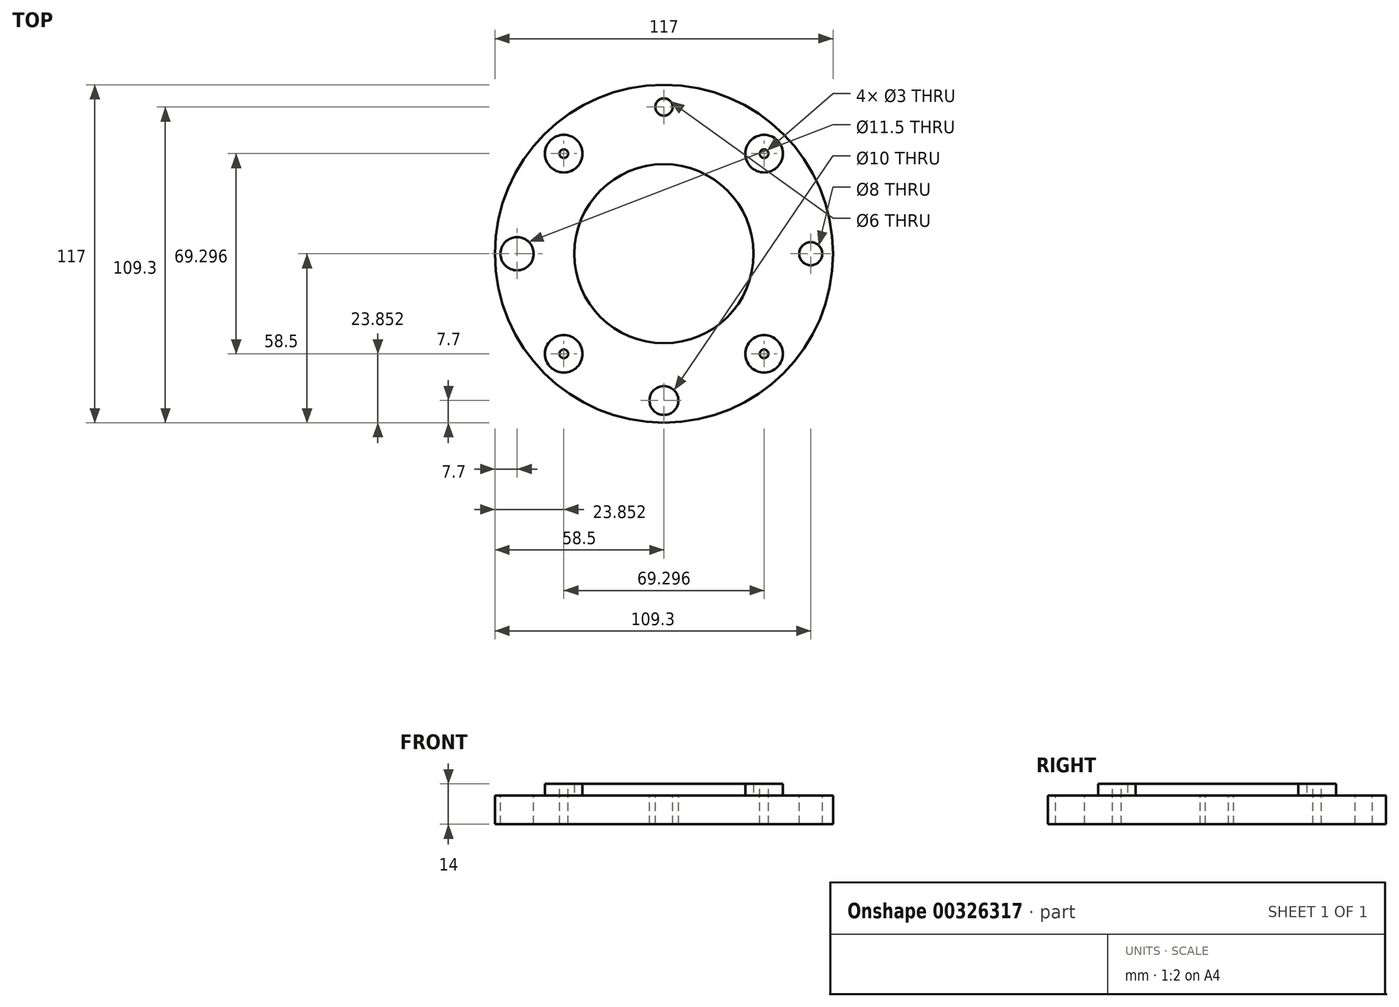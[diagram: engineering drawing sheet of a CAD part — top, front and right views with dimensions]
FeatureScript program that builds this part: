
annotation { "Feature Type Name" : "Feature", "Feature Type Description" : "" }
export const myFeature = defineFeature(function(context is Context, id is Id, definition is map)
    precondition{}
    {
        {
            var Q0;
            Q0=qCreatedBy(makeId("Top.planeOp"),FACE);
            var sketch = newSketch(context, id + "F0", { "sketchPlane" : qUnion([Q0])});
            skCircle(sketch, "E0", {"center": v(0, 0) * mm, "radius": 58.5 * mm});
            skCircle(sketch, "E1", {"center": v(0, 0) * mm, "radius": 50.8 * mm, "construction": true});
            skCircle(sketch, "E2", {"center": v(0, 50.8) * mm, "radius": 5.75 * mm, "construction": true});
            skCircle(sketch, "E3.1.0", {"center": v(-50.8, 0) * mm, "radius": 5.75 * mm, "construction": true});
            skCircle(sketch, "E3.2.0", {"center": v(0, -50.8) * mm, "radius": 5.75 * mm, "construction": true});
            skCircle(sketch, "E3.3.0", {"center": v(50.8, 0) * mm, "radius": 5.75 * mm, "construction": true});
            skCircle(sketch, "E4", {"center": v(0, 0) * mm, "radius": 61.85 * mm, "construction": true});
            skCircle(sketch, "E5", {"center": v(0, 0) * mm, "radius": 63.5 * mm});
            skCircle(sketch, "E6", {"center": v(0, 0) * mm, "radius": 49 * mm, "construction": true});
            skCircle(sketch, "E7", {"center": v(34.65, 34.65) * mm, "radius": 6.5 * mm});
            skCircle(sketch, "E8.1.0", {"center": v(-34.65, 34.65) * mm, "radius": 6.5 * mm});
            skCircle(sketch, "E8.2.0", {"center": v(-34.65, -34.65) * mm, "radius": 6.5 * mm});
            skCircle(sketch, "E8.3.0", {"center": v(34.65, -34.65) * mm, "radius": 6.5 * mm});
            skCircle(sketch, "E9", {"center": v(0, 0) * mm, "radius": 35.25 * mm, "construction": true});
            skCircle(sketch, "E10", {"center": v(0, 0) * mm, "radius": 31 * mm});
            skCircle(sketch, "E11", {"center": v(49, 0) * mm, "radius": 4.25 * mm, "construction": true});
            skCircle(sketch, "E12", {"center": v(-49, 0) * mm, "radius": 4.25 * mm, "construction": true});
            skCircle(sketch, "E13", {"center": v(0, 50.8) * mm, "radius": 3 * mm});
            skCircle(sketch, "E14", {"center": v(50.8, 0) * mm, "radius": 4 * mm});
            skCircle(sketch, "E15", {"center": v(0, -50.8) * mm, "radius": 5 * mm});
            skCircle(sketch, "E16", {"center": v(-50.8, 0) * mm, "radius": 5.75 * mm});
            skCircle(sketch, "E17", {"center": v(-34.65, 34.65) * mm, "radius": 1.5 * mm});
            skCircle(sketch, "E18", {"center": v(34.65, 34.65) * mm, "radius": 1.5 * mm});
            skCircle(sketch, "E19", {"center": v(-34.65, -34.65) * mm, "radius": 1.5 * mm});
            skCircle(sketch, "E20", {"center": v(34.65, -34.65) * mm, "radius": 1.5 * mm});
            skCircle(sketch, "E21", {"center": v(0, 50.8) * mm, "radius": 9 * mm, "construction": true});
            skSolve(sketch);
        }
        {
            var Q0;
            Q0=makeQuery(id+"F0.imprint","IMPRINT",FACE,{"disambiguationData":[TD([[makeQuery(id+"F0.imprint","IMPRINT",EDGE,{"derivedFrom":sQuery(id+"F0.wireOp",EDGE,"E0")}),1.0]])]});
            var Q1;
            Q1=makeQuery(id+"F0.imprint","IMPRINT",FACE,{"disambiguationData":[TD([[makeQuery(id+"F0.imprint","IMPRINT",EDGE,{"derivedFrom":sQuery(id+"F0.wireOp",EDGE,"E8.1.0")}),1.0]])]});
            var Q2;
            Q2=makeQuery(id+"F0.imprint","IMPRINT",FACE,{"disambiguationData":[TD([[makeQuery(id+"F0.imprint","IMPRINT",EDGE,{"derivedFrom":sQuery(id+"F0.wireOp",EDGE,"E7")}),1.0]])]});
            var Q3;
            Q3=makeQuery(id+"F0.imprint","IMPRINT",FACE,{"disambiguationData":[TD([[makeQuery(id+"F0.imprint","IMPRINT",EDGE,{"derivedFrom":sQuery(id+"F0.wireOp",EDGE,"E8.3.0")}),1.0]])]});
            var Q4;
            Q4=makeQuery(id+"F0.imprint","IMPRINT",FACE,{"disambiguationData":[TD([[makeQuery(id+"F0.imprint","IMPRINT",EDGE,{"derivedFrom":sQuery(id+"F0.wireOp",EDGE,"E8.2.0")}),1.0]])]});
            var Q5;
            Q5=makeQuery(id+"F0.imprint","IMPRINT",FACE,{"disambiguationData":[TD([[makeQuery(id+"F0.imprint","IMPRINT",EDGE,{"derivedFrom":sQuery(id+"F0.wireOp",EDGE,"E10")}),1.0]])]});
            extrude(context, id + "F1", {"entities" : qUnion([Q0, Q1, Q2, Q3, Q4, Q5]), "oppositeDirection" : true, "depth" : 10 * mm});
        }
        {
            var Q0;
            Q0=makeQuery(id+"F0.imprint","IMPRINT",FACE,{"disambiguationData":[TD([[makeQuery(id+"F0.imprint","IMPRINT",EDGE,{"derivedFrom":sQuery(id+"F0.wireOp",EDGE,"E8.1.0")}),1.0]])]});
            var Q1;
            Q1=makeQuery(id+"F0.imprint","IMPRINT",FACE,{"disambiguationData":[TD([[makeQuery(id+"F0.imprint","IMPRINT",EDGE,{"derivedFrom":sQuery(id+"F0.wireOp",EDGE,"E7")}),1.0]])]});
            var Q2;
            Q2=makeQuery(id+"F0.imprint","IMPRINT",FACE,{"disambiguationData":[TD([[makeQuery(id+"F0.imprint","IMPRINT",EDGE,{"derivedFrom":sQuery(id+"F0.wireOp",EDGE,"E8.3.0")}),1.0]])]});
            var Q3;
            Q3=makeQuery(id+"F0.imprint","IMPRINT",FACE,{"disambiguationData":[TD([[makeQuery(id+"F0.imprint","IMPRINT",EDGE,{"derivedFrom":sQuery(id+"F0.wireOp",EDGE,"E8.2.0")}),1.0]])]});
            var Q4;
            Q4=makeQuery(id+"F0.imprint","IMPRINT",FACE,{"disambiguationData":[TD([[makeQuery(id+"F0.imprint","IMPRINT",EDGE,{"derivedFrom":sQuery(id+"F0.wireOp",EDGE,"E10")}),1.0]])]});
            extrude(context, id + "F2", {"entities" : qUnion([Q0, Q1, Q2, Q3, Q4]), "operationType" : NewBodyOperationType.ADD, "depth" : 4 * mm});
        }
    });
